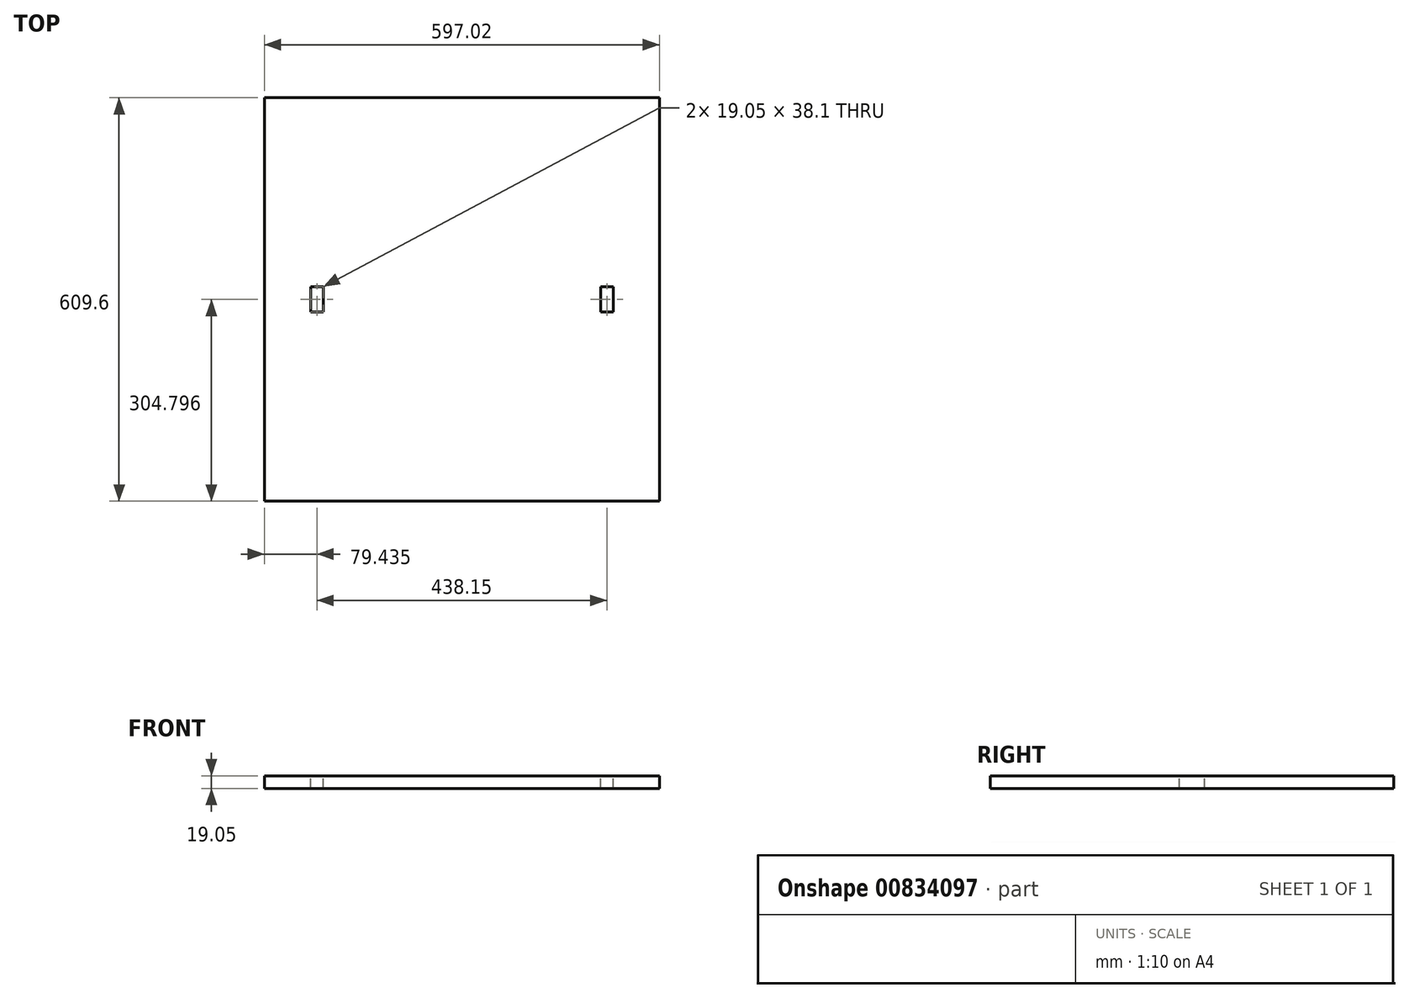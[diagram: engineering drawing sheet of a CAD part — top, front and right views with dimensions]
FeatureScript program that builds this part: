
annotation { "Feature Type Name" : "Feature", "Feature Type Description" : "" }
export const myFeature = defineFeature(function(context is Context, id is Id, definition is map)
    precondition{}
    {
        {
            var Q0;
            Q0=qCreatedBy(makeId("Top.planeOp"),FACE);
            var sketch = newSketch(context, id + "F0", { "sketchPlane" : qUnion([Q0])});
            skLineSegment(sketch, "E0.bottom", {"start": v(120.9, -266.9) * mm, "end": v(-476.12, -266.9) * mm});
            skLineSegment(sketch, "E0.top", {"start": v(120.9, 342.7) * mm, "end": v(-476.12, 342.7) * mm});
            skLineSegment(sketch, "E0.left", {"start": v(120.9, -266.9) * mm, "end": v(120.9, 342.7) * mm});
            skLineSegment(sketch, "E0.right", {"start": v(-476.12, -266.9) * mm, "end": v(-476.12, 342.7) * mm});
            skSolve(sketch);
        }
        {
            var Q0;
            Q0=makeQuery(id+"F0.imprint","IMPRINT",FACE,{"disambiguationData":[TD([[makeQuery(id+"F0.imprint","IMPRINT",EDGE,{"derivedFrom":sQuery(id+"F0.wireOp",EDGE,"E0.bottom")}),-1.0]])]});
            var Q1;
            Q1 = qConstructionFilter(qBodyType(qCreatedBy(id + "F0" ,EDGE), BodyType.WIRE), ConstructionObject.NO);
            extrude(context, id + "F1", {"entities" : qUnion([Q0]), "surfaceEntities" : qUnion([Q1]), "depth" : 19.05 * mm, "offsetDistance" : 25.4 * mm});
        }
        {
            var Q0;
            Q0=makeQuery(id+"F1.opExtrude","CAP_FACE",FACE,{"disambiguationData":[OSD([sQuery(id+"F0.wireOp",EDGE,"E0.bottom"),sQuery(id+"F0.wireOp",EDGE,"E0.top"),sQuery(id+"F0.wireOp",EDGE,"E0.left"),sQuery(id+"F0.wireOp",EDGE,"E0.right")])],"isStart":false});
            var sketch = newSketch(context, id + "F2", { "sketchPlane" : qUnion([Q0])});
            skLineSegment(sketch, "E1", {"start": v(-476.12, 37.9) * mm, "end": v(120.9, 37.9) * mm, "construction": true});
            skLineSegment(sketch, "E2.bottom", {"start": v(-387.16, 18.85) * mm, "end": v(-406.21, 18.85) * mm});
            skLineSegment(sketch, "E2.top", {"start": v(-387.16, 56.95) * mm, "end": v(-406.21, 56.95) * mm});
            skLineSegment(sketch, "E2.left", {"start": v(-387.16, 18.85) * mm, "end": v(-387.16, 56.95) * mm});
            skLineSegment(sketch, "E2.right", {"start": v(-406.21, 18.85) * mm, "end": v(-406.21, 56.95) * mm});
            skPoint(sketch, "E2.middle", {"position": v(-396.69, 37.9) * mm});
            skLineSegment(sketch, "E3", {"start": v(-177.61, 342.7) * mm, "end": v(-177.61, -266.9) * mm, "construction": true});
            skLineSegment(sketch, "E4.MirrorCS", {"start": v(50.99, 18.85) * mm, "end": v(50.99, 56.95) * mm});
            skPoint(sketch, "E5.MirrorP", {"position": v(41.46, 37.9) * mm});
            skLineSegment(sketch, "E6.MirrorCS", {"start": v(31.94, 18.85) * mm, "end": v(31.94, 56.95) * mm});
            skLineSegment(sketch, "E7.MirrorCS", {"start": v(31.94, 18.85) * mm, "end": v(50.99, 18.85) * mm});
            skLineSegment(sketch, "E8.MirrorCS", {"start": v(31.94, 56.95) * mm, "end": v(50.99, 56.95) * mm});
            skSolve(sketch);
        }
        {
            var Q0;
            Q0 = qSketchRegion(id + "F2", true);
            extrude(context, id + "F3", {"entities" : qUnion([Q0]), "operationType" : NewBodyOperationType.REMOVE, "oppositeDirection" : true, "depth" : 25.4 * mm, "offsetDistance" : 25.4 * mm});
        }
    });
